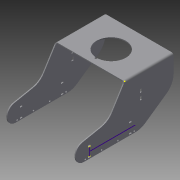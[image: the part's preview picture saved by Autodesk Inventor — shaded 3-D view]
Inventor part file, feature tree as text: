
AUTODESK INVENTOR PART (.ipt)
format: ipt  version: 2015 (Build 190159000, 159)  size: 398,848 bytes
history: native  units: mm
features: sketch x5, other x2, extrude x1
ambient origin geometry x8: Origin, YZ Plane, XZ Plane, XY Plane, X Axis, Y Axis, Z Axis, Center Point
bodies: Body1 (feature_tree)
feature tree (8):
  extrude  "Extrusion25"  Depth=3.0mm TaperAngle=0.0deg
  other  "Bend Part37"
  other  "Bend Part38"
  sketch  "Sketch47"  dims[d813=3.0mm d814=90.0deg]
  sketch  "Sketch48"
  sketch  "Sketch44"  dims[d19=5.0mm d127=97.0mm d151=5.0mm d163=5.0mm d222=5.0mm d248=40.0mm d294=25.0mm d324=5.0mm d326=25.0mm d329=25.0mm d344=6.0mm d358=6.0mm d404=5.0mm d406=45.0mm d445=20.0mm d446=30.0mm d448=45.0deg d460=5.606189mm d463=30.0deg d467=42.0mm d468=36.0mm d469=150.0deg d483=12.0mm d486=42.0mm d487=150.0deg d488=36.0mm d489=150.0deg d528=20.0mm d530=65.0mm]
  sketch  "Sketch45"  dims[d726=80.0mm d727=50.0mm d728=200.0mm d729=100.0mm d730=70.0mm d731=180.0mm d732=20.0mm d733=100.0mm d734=50.0mm d735=50.0mm d736=25.0mm d737=5.0mm d738=5.0mm d739=150.0mm d740=5.0mm d741=5.0mm d742=30.0mm d743=10.0mm d744=6.0mm d745=97.0mm d746=73.0mm d747=4.0mm d748=8.0mm d749=8.0mm d750=7.0mm d751=4.0mm d752=8.0mm d753=8.0mm d754=1.0mm d755=8.0mm d756=4.0mm d757=7.0mm d758=8.0mm d759=4.0mm d760=8.0mm d761=30.0mm d762=8.0mm d763=1.0mm d764=30.0mm d765=8.0mm d766=4.0mm d767=8.0mm d768=4.0mm d769=30.0mm d770=7.0mm d771=5.0mm d772=8.0mm d773=4.0mm d774=8.0mm d775=4.0mm d776=30.0mm d777=7.0mm d778=5.0mm d779=90.0mm d780=97.0mm d781=6.0mm d782=10.0mm d783=73.0mm d784=65.0mm d785=100.0mm d786=200.0mm d787=5.0mm d788=2.5mm d789=50.0mm d790=2.5mm d791=5.0mm d792=5.0mm d793=50.0mm d794=5.0mm d795=5.0mm d796=50.0mm d797=5.0mm d798=5.0mm d799=50.0mm d800=5.0mm d801=5.0mm d802=50.0mm d803=10.0mm d804=6.0mm d805=10.0mm d806=10.0mm d807=10.0mm d808=6.0mm d809=3.0mm d810=0.0mm]
  sketch  "Sketch46"  dims[d811=3.0mm d812=90.0deg]
